# Revit family: HL3(DX3)-20-75
name_source: partatom
category: Mechanical Equipment
revit_build: Autodesk Revit Architecture 2012 (Build: 20110309_2315(x64)
units: mm (PartAtom-declared; Revit-internal decimal feet)

## types (1)
- HL3(DX3)-20-75
    Below Clearance = 5' - 0"
    Frequency = 60 Hz
    Gas Type = N or LP
    Heat Gain (High Fire) = 75000.0 Btu/h
    Heat Gain (Low Fire) = 50000.0 Btu/h
    Length = 21' - 9"
    Manufacturer = Detroit Radiant Products Company
    Material (Combustion Tube) = Black Coated Aluminized Steel
    Material (Radiant Tubes) = Black Coated Aluminized Steel
    Model = HL3(DX3)-20-75
    Note = Low fire input for HL3 series only
    Recommended Mounting Height = 12' to 20'
    Side Clearance = 0' - 9"
    Stage = HL3 (Two), DX3 (Single)
    Top Clearance = 0' - 6"
    URL = www.DetroitRadiant.com
    Voltage = 120 V
    Weight = 120 Pounds

## geometry (parser evidence)
native form markers: Sweep x7
no freeform markers — native parametric forms only
